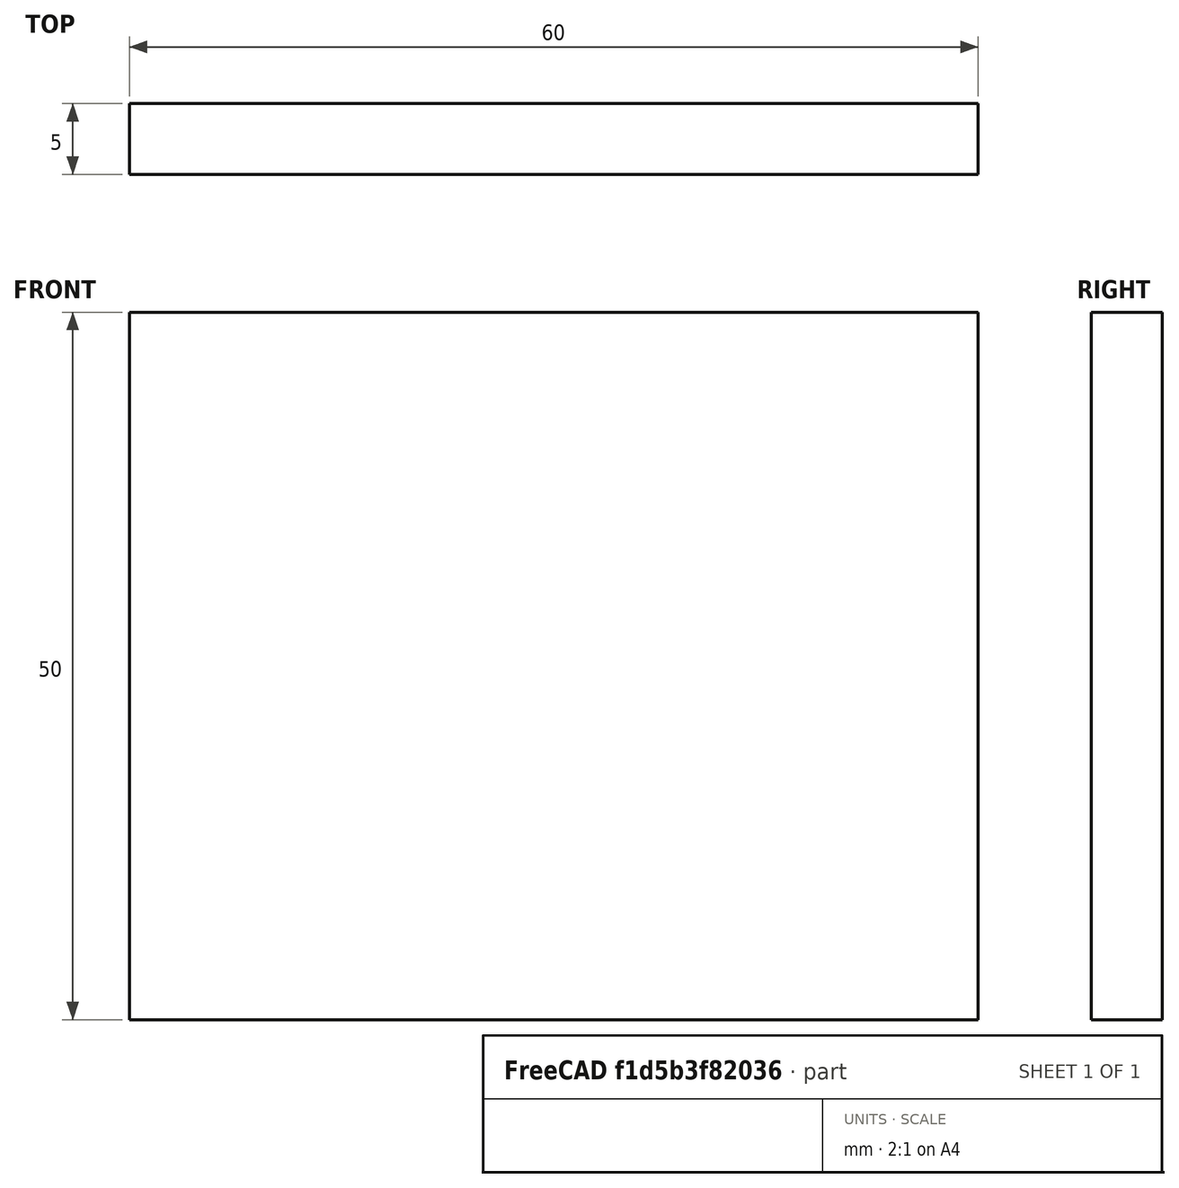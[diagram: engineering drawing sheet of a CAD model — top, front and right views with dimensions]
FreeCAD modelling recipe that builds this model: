
FCSTD DOCUMENT  (FreeCAD 0.15R4671 (Git))
Label: Flat Bar 60x5 EN10058 S235JR
License: All rights reserved
LicenseURL: http://en.wikipedia.org/wiki/All_rights_reserved
objects: Sketcher::SketchObject×1, Part::Extrusion×1
note: 2 computed .brp shape members not serialized (recipe doc carries the construction recipe); baked Part::Feature solids carry a one-line shape summary decoded from their .brp

FEATURE [Sketcher::SketchObject] Sketch
  sketch-geometry (4):
    g0: LineSegment StartX=-30 StartY=-2.5 StartZ=0 EndX=30 EndY=-2.5 EndZ=0
    g1: LineSegment StartX=30 StartY=-2.5 StartZ=0 EndX=30 EndY=2.5 EndZ=0
    g2: LineSegment StartX=30 StartY=2.5 StartZ=0 EndX=-30 EndY=2.5 EndZ=0
    g3: LineSegment StartX=-30 StartY=2.5 StartZ=0 EndX=-30 EndY=-2.5 EndZ=0
  constraints (12):
    c: Coincident(g0,g1)
    c: Coincident(g1,g2)
    c: Coincident(g2,g3)
    c: Coincident(g3,g0)
    c: Horizontal(g0)
    c: Horizontal(g2)
    c: Vertical(g1)
    c: Vertical(g3)
    c: Symmetric(g1,g2,g-2)
    c: Symmetric(g0,g1,g-1)
    c: DistanceY(g1) = 5
    c: DistanceX(g0) = 60
FEATURE [Part::Extrusion] Extrude  label="Flat Bar 60x5 EN10058 S235JR"
  Base = -> Sketch
  Dir = (0,0,50)
  Solid = true
